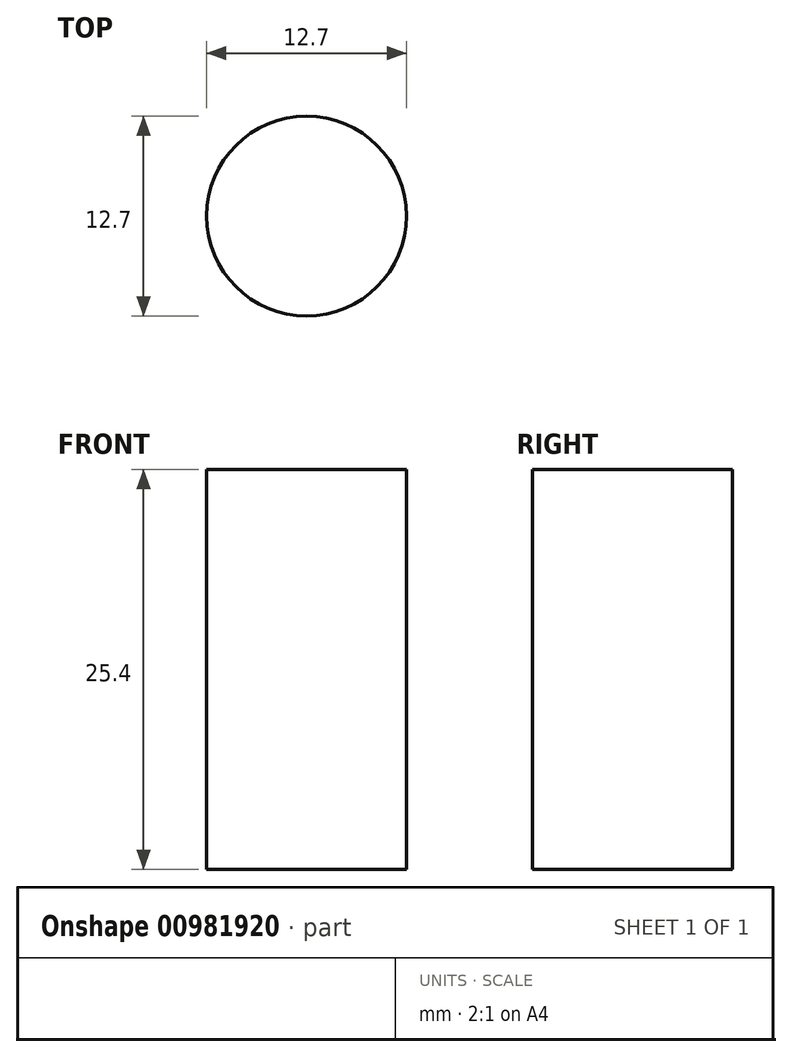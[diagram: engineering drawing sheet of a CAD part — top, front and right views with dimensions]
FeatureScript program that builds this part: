
annotation { "Feature Type Name" : "Feature", "Feature Type Description" : "" }
export const myFeature = defineFeature(function(context is Context, id is Id, definition is map)
    precondition{}
    {
        {
            var Q0;
            Q0=qCreatedBy(makeId("Top.planeOp"),FACE);
            var sketch = newSketch(context, id + "F0", { "sketchPlane" : qUnion([Q0])});
            skCircle(sketch, "E0", {"center": v(0, 0) * mm, "radius": 6.35 * mm});
            skSolve(sketch);
        }
        {
            var Q0;
            Q0 = qSketchRegion(id + "F0", true);
            extrude(context, id + "F1", {"entities" : qUnion([Q0]), "depth" : 25.4 * mm, "offsetDistance" : 25.4 * mm});
        }
    });
